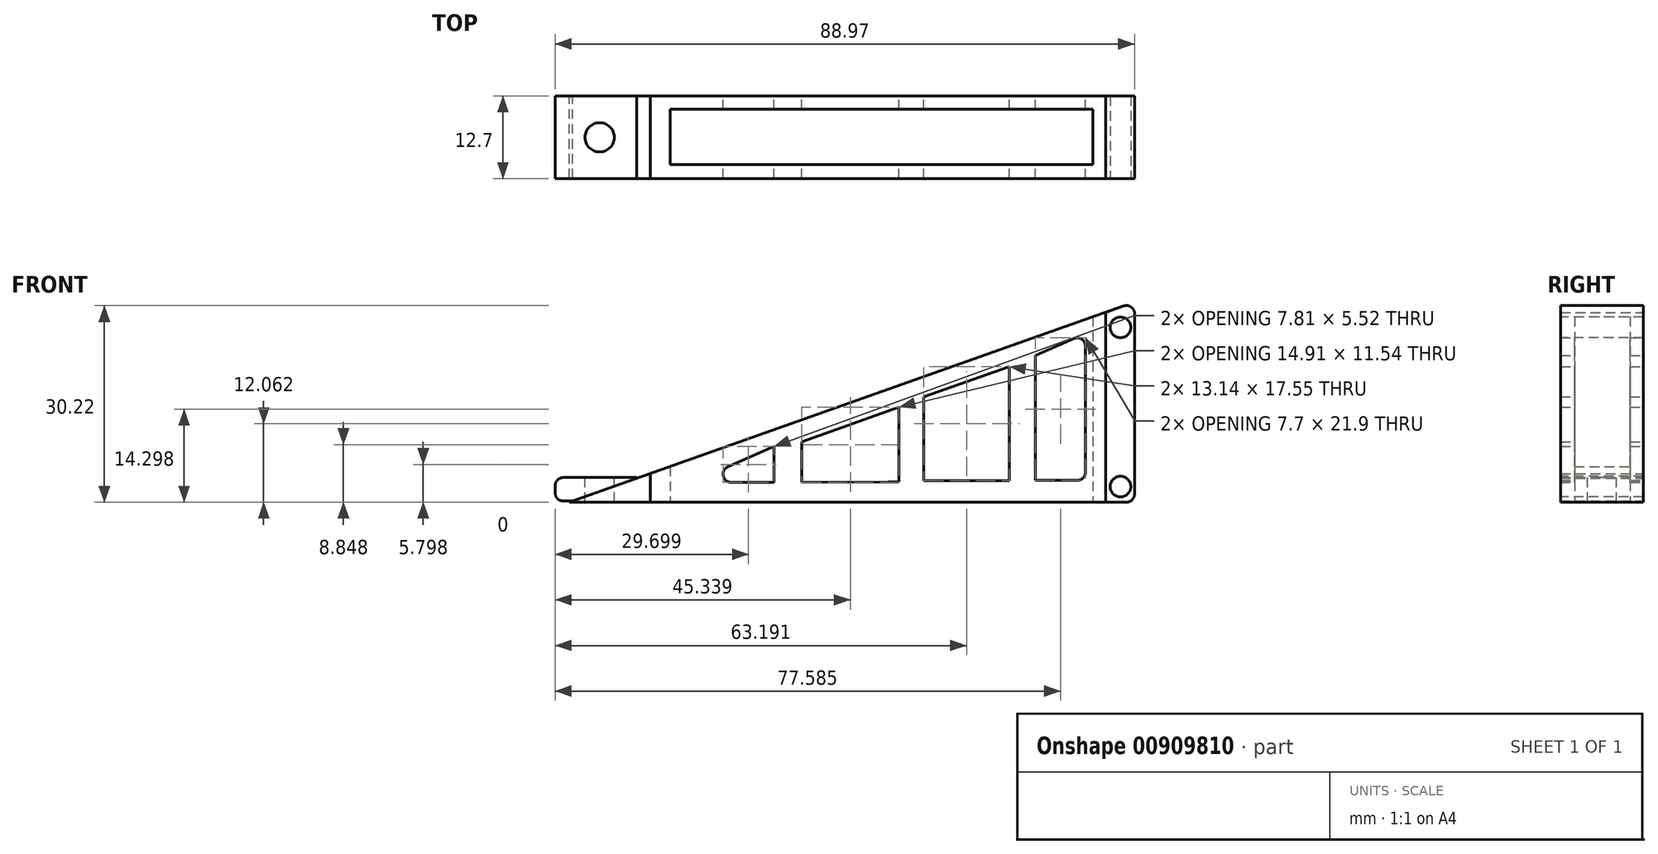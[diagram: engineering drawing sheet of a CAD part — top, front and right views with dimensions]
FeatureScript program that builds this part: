
annotation { "Feature Type Name" : "Feature", "Feature Type Description" : "" }
export const myFeature = defineFeature(function(context is Context, id is Id, definition is map)
    precondition{}
    {
        {
            var Q0;
            Q0=qCreatedBy(makeId("Front.planeOp"),FACE);
            var sketch = newSketch(context, id + "F0", { "sketchPlane" : qUnion([Q0])});
            skLineSegment(sketch, "E0", {"start": v(-39.69, -25.93) * mm, "end": v(45.82, -25.93) * mm});
            skLineSegment(sketch, "E1", {"start": v(47.1, -24.66) * mm, "end": v(47.1, 3.02) * mm});
            skLineSegment(sketch, "E2", {"start": v(45.4, 4.22) * mm, "end": v(-39.69, -25.93) * mm});
            skPoint(sketch, "E3.visualSharp", {"position": v(47.1, 4.82) * mm});
            skArc(sketch, "E3.filletArc", {"start": v(47.1, 3.02) * mm, "mid": v(46.56, 4.06) * mm, "end": v(45.4, 4.22) * mm});
            skPoint(sketch, "E4.visualSharp", {"position": v(47.1, -25.93) * mm});
            skArc(sketch, "E4.filletArc", {"start": v(45.82, -25.93) * mm, "mid": v(46.72, -25.56) * mm, "end": v(47.1, -24.66) * mm});
            skSolve(sketch);
        }
        {
            var Q0;
            Q0 = qSketchRegion(id + "F0", true);
            extrude(context, id + "F1", {"entities" : qUnion([Q0]), "endBound" : BoundingType.SYMMETRIC, "depth" : 12.7 * mm, "offsetDistance" : 25.4 * mm});
        }
        {
            var Q0;
            Q0=makeQuery(id+"F1.opExtrude","SWEPT_FACE",FACE,{"disambiguationData":[OSD([sQuery(id+"F0.wireOp",EDGE,"E0")])]});
            var sketch = newSketch(context, id + "F2", { "sketchPlane" : qUnion([Q0])});
            skLineSegment(sketch, "E5.bottom", {"start": v(-27.24, 7.94) * mm, "end": v(42.65, 7.94) * mm});
            skLineSegment(sketch, "E5.top", {"start": v(-27.24, -8.19) * mm, "end": v(42.65, -8.19) * mm});
            skLineSegment(sketch, "E5.left", {"start": v(-27.24, 7.94) * mm, "end": v(-27.24, -8.19) * mm});
            skLineSegment(sketch, "E5.right", {"start": v(42.65, 7.94) * mm, "end": v(42.65, -8.19) * mm});
            skSolve(sketch);
        }
        {
            var Q0;
            Q0 = qSketchRegion(id + "F2", true);
            extrude(context, id + "F3", {"entities" : qUnion([Q0]), "operationType" : NewBodyOperationType.REMOVE, "endBound" : BoundingType.SYMMETRIC, "oppositeDirection" : true, "depth" : 254 * mm, "offsetDistance" : 25.4 * mm});
        }
        {
            var Q0;
            Q0=qCreatedBy(makeId("Front.planeOp"),FACE);
            var sketch = newSketch(context, id + "F4", { "sketchPlane" : qUnion([Q0])});
            skLineSegment(sketch, "E6.bottom", {"start": v(-29.37, -25.74) * mm, "end": v(-40.61, -25.74) * mm});
            skLineSegment(sketch, "E6.top", {"start": v(-29.37, -22.14) * mm, "end": v(-40.61, -22.14) * mm});
            skLineSegment(sketch, "E6.left", {"start": v(-29.37, -25.74) * mm, "end": v(-29.37, -22.14) * mm});
            skLineSegment(sketch, "E6.right", {"start": v(-41.88, -24.47) * mm, "end": v(-41.88, -23.4) * mm});
            skPoint(sketch, "E7.visualSharp", {"position": v(-41.88, -22.14) * mm});
            skArc(sketch, "E7.filletArc", {"start": v(-40.61, -22.14) * mm, "mid": v(-41.51, -22.5) * mm, "end": v(-41.88, -23.4) * mm});
            skPoint(sketch, "E8.visualSharp", {"position": v(-41.88, -25.74) * mm});
            skArc(sketch, "E8.filletArc", {"start": v(-41.88, -24.47) * mm, "mid": v(-41.51, -25.37) * mm, "end": v(-40.61, -25.74) * mm});
            skSolve(sketch);
        }
        {
            var Q0;
            Q0 = qSketchRegion(id + "F4", true);
            extrude(context, id + "F5", {"entities" : qUnion([Q0]), "operationType" : NewBodyOperationType.ADD, "endBound" : BoundingType.SYMMETRIC, "depth" : 12.7 * mm, "offsetDistance" : 25.4 * mm});
        }
        {
            var Q0;
            Q0=makeQuery(id+"F5.opExtrude","SWEPT_FACE",FACE,{"disambiguationData":[OSD([sQuery(id+"F4.wireOp",EDGE,"E6.top")])]});
            var sketch = newSketch(context, id + "F6", { "sketchPlane" : qUnion([Q0])});
            skPoint(sketch, "E9.centerSnap0", {"position": v(-35, -6.35) * mm});
            skCircle(sketch, "E10", {"center": v(-35.04, 0) * mm, "radius": 2.25 * mm});
            skSolve(sketch);
        }
        {
            var Q0;
            Q0 = qSketchRegion(id + "F6", true);
            extrude(context, id + "F7", {"entities" : qUnion([Q0]), "operationType" : NewBodyOperationType.REMOVE, "endBound" : BoundingType.SYMMETRIC, "oppositeDirection" : true, "depth" : 254 * mm, "offsetDistance" : 25.4 * mm});
        }
        {
            var Q0;
            Q0=makeQuery(id+"F0.imprint","IMPRINT",FACE,{"disambiguationData":[TD([[makeQuery(id+"F0.imprint","IMPRINT",EDGE,{"derivedFrom":sQuery(id+"F0.wireOp",EDGE,"E0")}),1.0]])]});
            extrude(context, id + "F8", {"entities" : qUnion([Q0]), "endBound" : BoundingType.SYMMETRIC, "depth" : 12.7 * mm, "offsetDistance" : 25.4 * mm});
        }
        {
            var Q0;
            Q0=makeQuery(id+"F8.opExtrude","SWEPT_FACE",FACE,{"disambiguationData":[OSD([sQuery(id+"F0.wireOp",EDGE,"E0")])]});
            var sketch = newSketch(context, id + "F9", { "sketchPlane" : qUnion([Q0])});
            skLineSegment(sketch, "E11.bottom", {"start": v(40.71, 4.21) * mm, "end": v(-24.2, 4.21) * mm});
            skLineSegment(sketch, "E11.top", {"start": v(40.71, -4.31) * mm, "end": v(-24.2, -4.31) * mm});
            skLineSegment(sketch, "E11.left", {"start": v(40.71, 4.21) * mm, "end": v(40.71, -4.31) * mm});
            skLineSegment(sketch, "E11.right", {"start": v(-24.2, 4.21) * mm, "end": v(-24.2, -4.31) * mm});
            skSolve(sketch);
        }
        {
            var Q0;
            Q0 = qSketchRegion(id + "F9", true);
            extrude(context, id + "F10", {"entities" : qUnion([Q0]), "operationType" : NewBodyOperationType.REMOVE, "endBound" : BoundingType.SYMMETRIC, "oppositeDirection" : true, "depth" : 254 * mm, "offsetDistance" : 25.4 * mm});
        }
        {
            var Q0;
            Q0=makeQuery(id+"F8.opExtrude","CAP_FACE",FACE,{"disambiguationData":[OSD([sQuery(id+"F0.wireOp",EDGE,"E0"),sQuery(id+"F0.wireOp",EDGE,"E1"),sQuery(id+"F0.wireOp",EDGE,"E2"),sQuery(id+"F0.wireOp",EDGE,"E3.filletArc"),sQuery(id+"F0.wireOp",EDGE,"E4.filletArc")])],"isStart":true});
            var sketch = newSketch(context, id + "F11", { "sketchPlane" : qUnion([Q0])});
            skLineSegment(sketch, "E12", {"start": v(-39.56, -21.31) * mm, "end": v(-39.56, -1.95) * mm});
            skLineSegment(sketch, "E13", {"start": v(-37.77, -0.79) * mm, "end": v(-31.85, -3.4) * mm});
            skLineSegment(sketch, "E14", {"start": v(-31.85, -3.4) * mm, "end": v(-31.85, -22.58) * mm});
            skLineSegment(sketch, "E15", {"start": v(-31.85, -22.58) * mm, "end": v(-38.29, -22.58) * mm});
            skLineSegment(sketch, "E16", {"start": v(-27.88, -22.64) * mm, "end": v(-27.88, -5.1) * mm});
            skLineSegment(sketch, "E17", {"start": v(-27.88, -5.1) * mm, "end": v(-14.74, -9.75) * mm});
            skLineSegment(sketch, "E18", {"start": v(-14.74, -9.75) * mm, "end": v(-14.74, -22.64) * mm});
            skLineSegment(sketch, "E19", {"start": v(-14.74, -22.64) * mm, "end": v(-27.88, -22.64) * mm});
            skLineSegment(sketch, "E20", {"start": v(-10.91, -22.83) * mm, "end": v(-10.91, -11.31) * mm});
            skLineSegment(sketch, "E21", {"start": v(-10.91, -11.31) * mm, "end": v(4, -16.64) * mm});
            skLineSegment(sketch, "E22", {"start": v(4, -16.64) * mm, "end": v(4, -22.85) * mm});
            skLineSegment(sketch, "E23", {"start": v(4, -22.85) * mm, "end": v(-9.28, -22.83) * mm});
            skLineSegment(sketch, "E24", {"start": v(-9.28, -22.83) * mm, "end": v(-10.91, -22.83) * mm});
            skLineSegment(sketch, "E25", {"start": v(8.27, -22.9) * mm, "end": v(8.27, -17.37) * mm});
            skLineSegment(sketch, "E26", {"start": v(8.27, -17.37) * mm, "end": v(15.34, -20.46) * mm});
            skLineSegment(sketch, "E27", {"start": v(14.83, -22.9) * mm, "end": v(8.27, -22.9) * mm});
            skPoint(sketch, "E28.visualSharp", {"position": v(-39.56, -22.58) * mm});
            skArc(sketch, "E28.filletArc", {"start": v(-39.56, -21.31) * mm, "mid": v(-39.18, -22.2) * mm, "end": v(-38.29, -22.58) * mm});
            skPoint(sketch, "E29.visualSharp", {"position": v(-39.56, 0) * mm});
            skArc(sketch, "E29.filletArc", {"start": v(-37.77, -0.79) * mm, "mid": v(-38.98, -0.88) * mm, "end": v(-39.56, -1.95) * mm});
            skPoint(sketch, "E30.visualSharp", {"position": v(20.9, -22.9) * mm});
            skArc(sketch, "E30.filletArc", {"start": v(14.83, -22.9) * mm, "mid": v(16.07, -21.88) * mm, "end": v(15.34, -20.46) * mm});
            skSolve(sketch);
        }
        {
            var Q0;
            Q0 = qSketchRegion(id + "F11", true);
            extrude(context, id + "F12", {"entities" : qUnion([Q0]), "operationType" : NewBodyOperationType.REMOVE, "endBound" : BoundingType.SYMMETRIC, "oppositeDirection" : true, "depth" : 254 * mm, "offsetDistance" : 25.4 * mm});
        }
        {
            var Q0;
            {var subQ0=sQuery(id+"F0.wireOp",EDGE,"E2");var subQ1=sQuery(id+"F0.wireOp",EDGE,"E1");var subQ2=sQuery(id+"F0.wireOp",EDGE,"E3.filletArc");var subQ3=sQuery(id+"F0.wireOp",EDGE,"E0");var subQ4=sQuery(id+"F0.wireOp",EDGE,"E4.filletArc");Q0=makeQuery(id+"F3.boolean.opBoolean","SPLIT",FACE,{"disambiguationData":[TD([makeQuery(id+"F1.opExtrude","SWEPT_FACE",FACE,{"disambiguationData":[OSD([subQ1])]})])],"derivedFrom":makeQuery(id+"F1.opExtrude","CAP_FACE",FACE,{"disambiguationData":[OSD([subQ3,subQ1,subQ0,subQ2,subQ4])],"isStart":false})});}
            var sketch = newSketch(context, id + "F13", { "sketchPlane" : qUnion([Q0])});
            skCircle(sketch, "E31", {"center": v(44.93, 0.93) * mm, "radius": 1.59 * mm});
            skCircle(sketch, "E32", {"center": v(44.93, -23.53) * mm, "radius": 1.59 * mm});
            skSolve(sketch);
        }
        {
            var Q0;
            Q0 = qSketchRegion(id + "F13", true);
            extrude(context, id + "F14", {"entities" : qUnion([Q0]), "operationType" : NewBodyOperationType.REMOVE, "oppositeDirection" : true, "depth" : 25.4 * mm, "offsetDistance" : 25.4 * mm});
        }
    });
